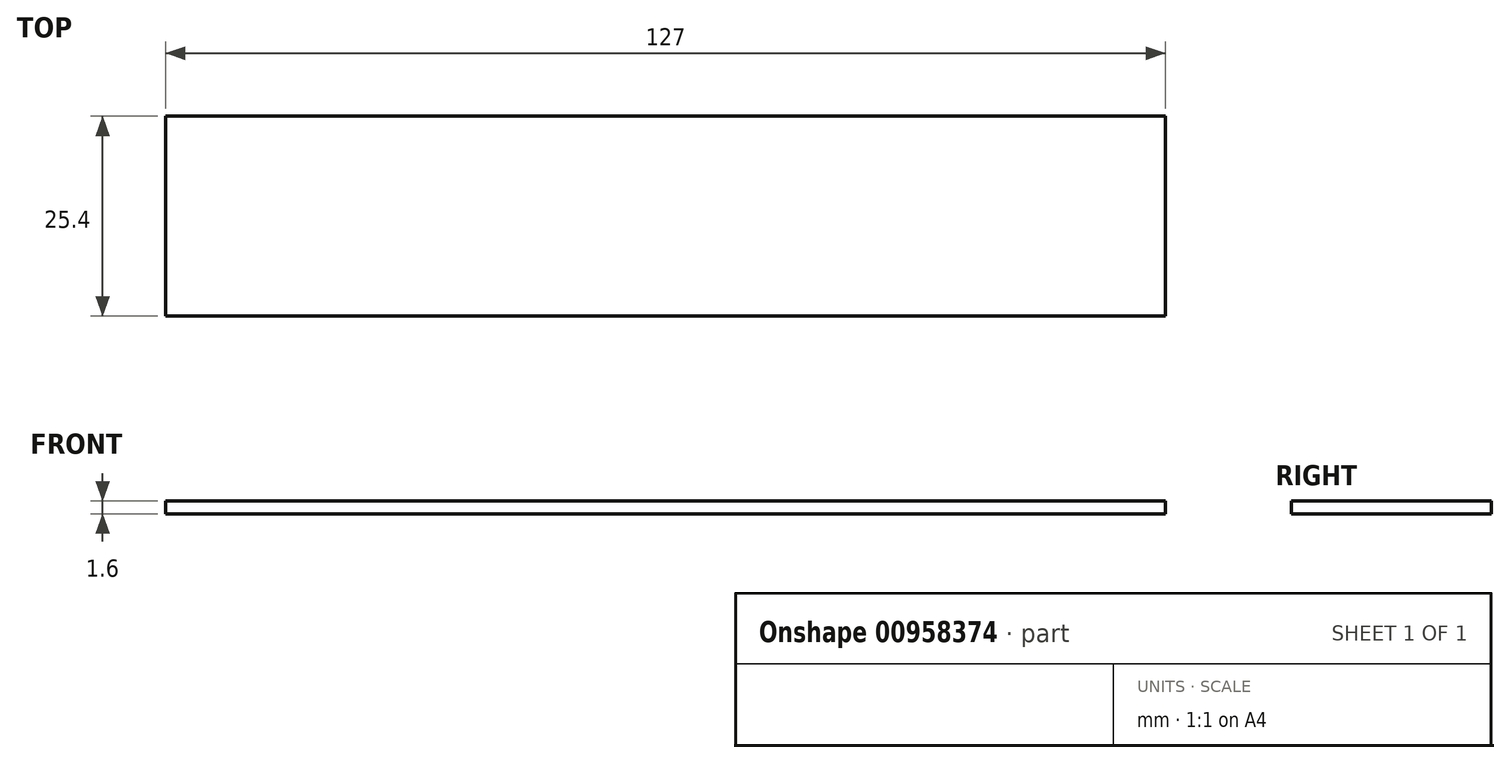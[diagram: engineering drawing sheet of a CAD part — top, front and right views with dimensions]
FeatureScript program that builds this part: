
annotation { "Feature Type Name" : "Feature", "Feature Type Description" : "" }
export const myFeature = defineFeature(function(context is Context, id is Id, definition is map)
    precondition{}
    {
        {
            var Q0;
            Q0=qCreatedBy(makeId("Front.planeOp"),FACE);
            var sketch = newSketch(context, id + "F0", { "sketchPlane" : qUnion([Q0])});
            skLineSegment(sketch, "E0", {"start": v(-70.5, -15.05) * mm, "end": v(56.5, -15.05) * mm});
            skLineSegment(sketch, "E1", {"start": v(56.5, -15.05) * mm, "end": v(56.5, -13.45) * mm});
            skLineSegment(sketch, "E2", {"start": v(56.5, -13.45) * mm, "end": v(-70.5, -13.45) * mm});
            skLineSegment(sketch, "E3", {"start": v(-70.5, -13.45) * mm, "end": v(-70.5, -15.05) * mm});
            skSolve(sketch);
        }
        {
            var Q0;
            Q0=makeQuery(id+"F0.imprint","IMPRINT",FACE,{"disambiguationData":[TD([[makeQuery(id+"F0.imprint","IMPRINT",EDGE,{"derivedFrom":sQuery(id+"F0.wireOp",EDGE,"E0")}),1.0]])]});
            extrude(context, id + "F1", {"entities" : qUnion([Q0]), "endBound" : BoundingType.SYMMETRIC, "depth" : 25.4 * mm, "offsetDistance" : 25.4 * mm});
        }
    });
